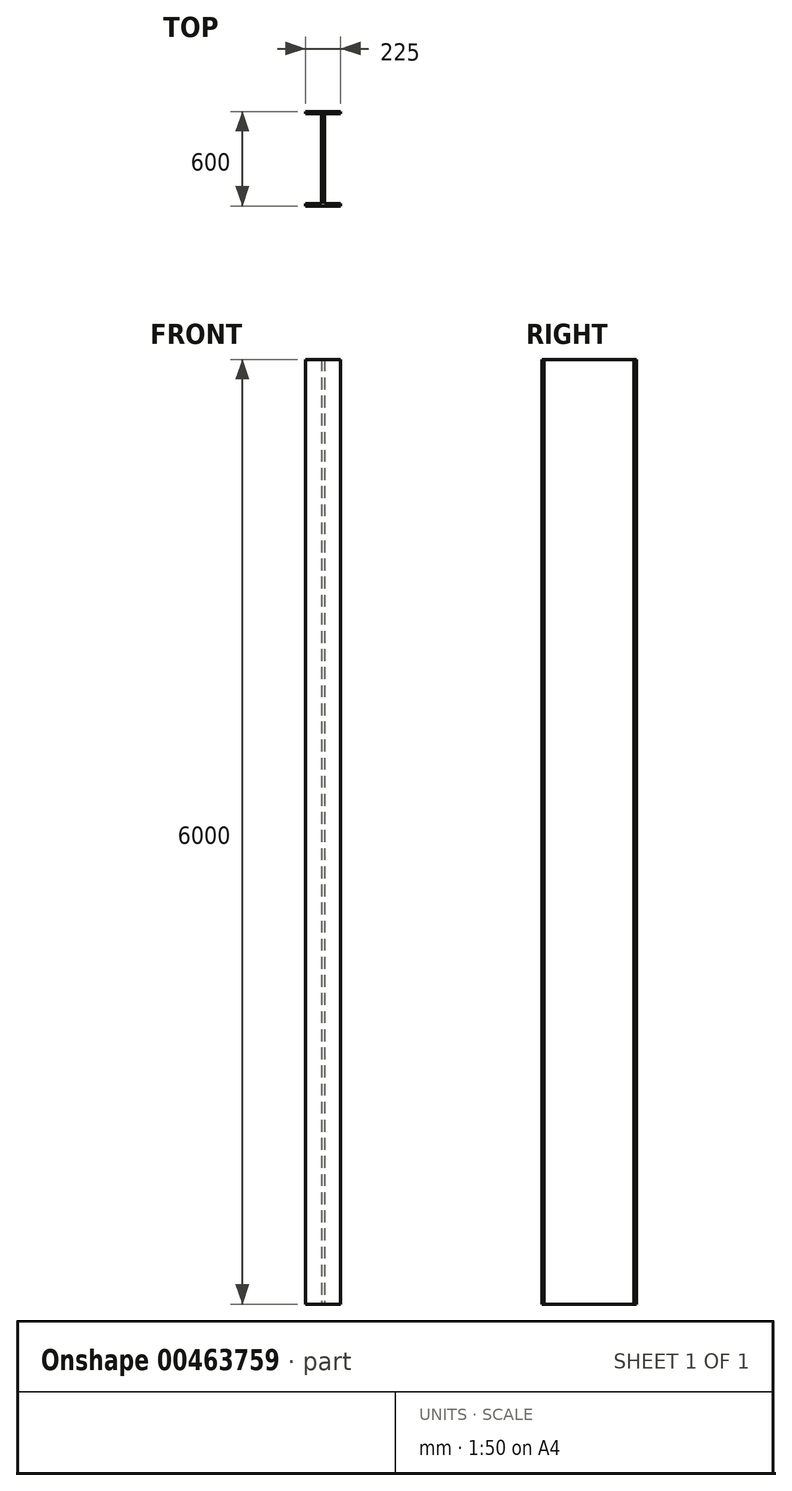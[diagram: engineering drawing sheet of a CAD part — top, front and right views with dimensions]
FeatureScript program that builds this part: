
annotation { "Feature Type Name" : "Feature", "Feature Type Description" : "" }
export const myFeature = defineFeature(function(context is Context, id is Id, definition is map)
    precondition{}
    {
        {
            var Q0;
            Q0=qCreatedBy(makeId("Top.planeOp"),FACE);
            var sketch = newSketch(context, id + "F0", { "sketchPlane" : qUnion([Q0]), "disableImprinting" : false});
            skLineSegment(sketch, "E0", {"start": v(0, 0) * mm, "end": v(225, 0) * mm});
            skLineSegment(sketch, "E1", {"start": v(225, 0) * mm, "end": v(225, 15) * mm});
            skLineSegment(sketch, "E2", {"start": v(225, 15) * mm, "end": v(122.5, 15) * mm});
            skLineSegment(sketch, "E3", {"start": v(122.5, 15) * mm, "end": v(122.5, 585) * mm});
            skLineSegment(sketch, "E4", {"start": v(122.5, 585) * mm, "end": v(225, 585) * mm});
            skLineSegment(sketch, "E5", {"start": v(225, 585) * mm, "end": v(225, 600) * mm});
            skLineSegment(sketch, "E6", {"start": v(225, 600) * mm, "end": v(0, 600) * mm});
            skLineSegment(sketch, "E7", {"start": v(0, 600) * mm, "end": v(0, 585) * mm});
            skLineSegment(sketch, "E8", {"start": v(0, 585) * mm, "end": v(102.5, 585) * mm});
            skLineSegment(sketch, "E9", {"start": v(102.5, 585) * mm, "end": v(102.5, 15) * mm});
            skLineSegment(sketch, "E10", {"start": v(102.5, 15) * mm, "end": v(0, 15) * mm});
            skLineSegment(sketch, "E11", {"start": v(0, 15) * mm, "end": v(0, 0) * mm});
            skSolve(sketch);
        }
        {
            var Q0;
            Q0 = qSketchRegion(id + "F0", true);
            extrude(context, id + "F1", {"entities" : qUnion([Q0]), "depth" : 6000 * mm});
        }
    });
